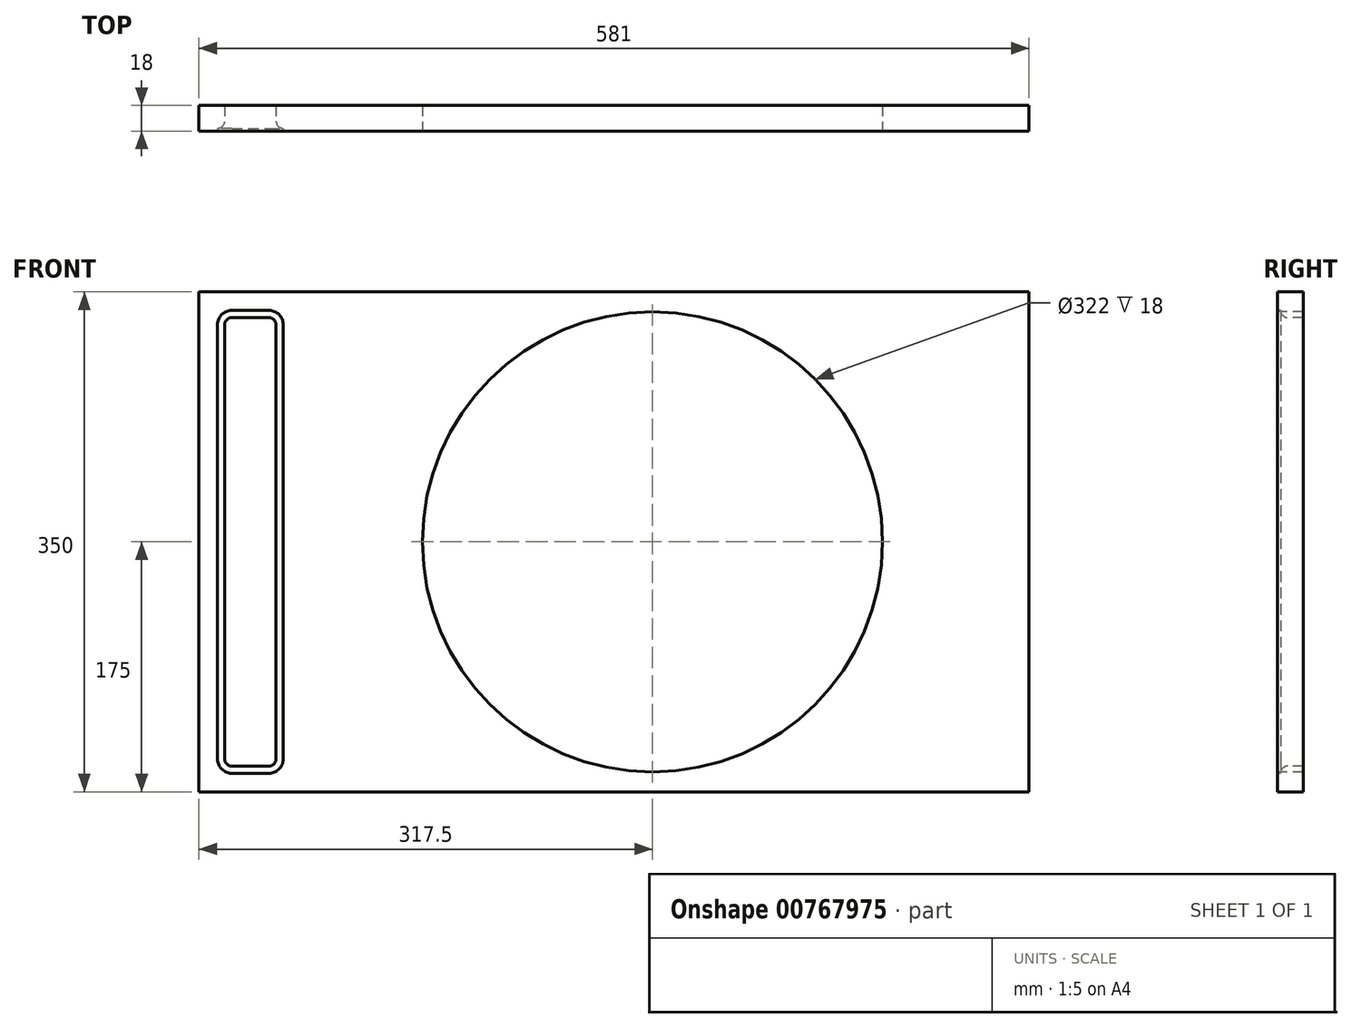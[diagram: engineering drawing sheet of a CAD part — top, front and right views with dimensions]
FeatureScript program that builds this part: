
annotation { "Feature Type Name" : "Feature", "Feature Type Description" : "" }
export const myFeature = defineFeature(function(context is Context, id is Id, definition is map)
    precondition{}
    {
        {
            var Q0;
            Q0=qCreatedBy(makeId("Front.planeOp"),FACE);
            var sketch = newSketch(context, id + "F0", { "sketchPlane" : qUnion([Q0])});
            skLineSegment(sketch, "E0.bottom", {"start": v(-290.5, -175) * mm, "end": v(290.5, -175) * mm});
            skLineSegment(sketch, "E0.top", {"start": v(-290.5, 175) * mm, "end": v(290.5, 175) * mm});
            skLineSegment(sketch, "E0.left", {"start": v(-290.5, -175) * mm, "end": v(-290.5, 175) * mm});
            skLineSegment(sketch, "E0.right", {"start": v(290.5, -175) * mm, "end": v(290.5, 175) * mm});
            skPoint(sketch, "E0.middle", {"position": v(0, 0) * mm});
            skLineSegment(sketch, "E1.bottom", {"start": v(-267.5, 157) * mm, "end": v(-241.5, 157) * mm});
            skLineSegment(sketch, "E1.top", {"start": v(-267.5, -157) * mm, "end": v(-241.5, -157) * mm});
            skLineSegment(sketch, "E1.left", {"start": v(-272.5, 152) * mm, "end": v(-272.5, -152) * mm});
            skLineSegment(sketch, "E1.right", {"start": v(-236.5, 152) * mm, "end": v(-236.5, -152) * mm});
            skLineSegment(sketch, "E2", {"start": v(-236.5, 157) * mm, "end": v(-236.5, 175) * mm, "construction": true});
            skLineSegment(sketch, "E3", {"start": v(-236.5, 175) * mm, "end": v(290.5, -175) * mm, "construction": true});
            skCircle(sketch, "E4", {"center": v(27, 0) * mm, "radius": 161 * mm});
            skPoint(sketch, "E5.visualSharp", {"position": v(-272.5, 157) * mm});
            skArc(sketch, "E5.filletArc", {"start": v(-267.5, 157) * mm, "mid": v(-271.04, 155.54) * mm, "end": v(-272.5, 152) * mm});
            skPoint(sketch, "E6.visualSharp", {"position": v(-236.5, 157) * mm});
            skArc(sketch, "E6.filletArc", {"start": v(-236.5, 152) * mm, "mid": v(-237.96, 155.54) * mm, "end": v(-241.5, 157) * mm});
            skPoint(sketch, "E7.visualSharp", {"position": v(-272.5, -157) * mm});
            skArc(sketch, "E7.filletArc", {"start": v(-272.5, -152) * mm, "mid": v(-271.04, -155.54) * mm, "end": v(-267.5, -157) * mm});
            skPoint(sketch, "E8.visualSharp", {"position": v(-236.5, -157) * mm});
            skArc(sketch, "E8.filletArc", {"start": v(-241.5, -157) * mm, "mid": v(-237.96, -155.54) * mm, "end": v(-236.5, -152) * mm});
            skSolve(sketch);
        }
        {
            var Q0;
            Q0 = qSketchRegion(id + "F0", true);
            extrude(context, id + "F1", {"entities" : qUnion([Q0]), "oppositeDirection" : true, "depth" : 18 * mm, "offsetDistance" : 25 * mm});
        }
        {
            var Q0;
            Q0=makeQuery(id+"F1.opExtrude","CAP_FACE",FACE,{"disambiguationData":[OSD([sQuery(id+"F0.wireOp",EDGE,"E0.bottom"),sQuery(id+"F0.wireOp",EDGE,"E0.top"),sQuery(id+"F0.wireOp",EDGE,"E0.left"),sQuery(id+"F0.wireOp",EDGE,"E0.right"),sQuery(id+"F0.wireOp",EDGE,"E1.bottom"),sQuery(id+"F0.wireOp",EDGE,"E1.top"),sQuery(id+"F0.wireOp",EDGE,"E1.left"),sQuery(id+"F0.wireOp",EDGE,"E1.right"),sQuery(id+"F0.wireOp",EDGE,"E4"),sQuery(id+"F0.wireOp",EDGE,"E5.filletArc"),sQuery(id+"F0.wireOp",EDGE,"E6.filletArc"),sQuery(id+"F0.wireOp",EDGE,"E7.filletArc"),sQuery(id+"F0.wireOp",EDGE,"E8.filletArc")])],"isStart":true});
            var sketch = newSketch(context, id + "F2", { "sketchPlane" : qUnion([Q0])});
            skLineSegment(sketch, "E9.bottom", {"start": v(-267.5, 162) * mm, "end": v(-241.5, 162) * mm});
            skLineSegment(sketch, "E9.top", {"start": v(-267.5, -162) * mm, "end": v(-241.5, -162) * mm});
            skLineSegment(sketch, "E9.left", {"start": v(-277.5, 152) * mm, "end": v(-277.5, -152) * mm});
            skLineSegment(sketch, "E9.right", {"start": v(-231.5, 152) * mm, "end": v(-231.5, -152) * mm});
            skPoint(sketch, "E10.visualSharp", {"position": v(-277.5, 162) * mm});
            skArc(sketch, "E10.filletArc", {"start": v(-267.5, 162) * mm, "mid": v(-274.57, 159.07) * mm, "end": v(-277.5, 152) * mm});
            skPoint(sketch, "E11.visualSharp", {"position": v(-231.5, 162) * mm});
            skArc(sketch, "E11.filletArc", {"start": v(-231.5, 152) * mm, "mid": v(-234.43, 159.07) * mm, "end": v(-241.5, 162) * mm});
            skPoint(sketch, "E12.visualSharp", {"position": v(-277.5, -162) * mm});
            skArc(sketch, "E12.filletArc", {"start": v(-277.5, -152) * mm, "mid": v(-274.57, -159.07) * mm, "end": v(-267.5, -162) * mm});
            skPoint(sketch, "E13.visualSharp", {"position": v(-231.5, -162) * mm});
            skArc(sketch, "E13.filletArc", {"start": v(-241.5, -162) * mm, "mid": v(-234.43, -159.07) * mm, "end": v(-231.5, -152) * mm});
            skSolve(sketch);
        }
        {
            var Q0;
            Q0 = qSketchRegion(id + "F2", true);
            extrude(context, id + "F3", {"entities" : qUnion([Q0]), "operationType" : NewBodyOperationType.REMOVE, "oppositeDirection" : true, "depth" : 2 * mm, "offsetDistance" : 25 * mm});
        }
        {
            var Q0;
            Q0=makeQuery(id+"F3.boolean.opBoolean","INTERSECT",EDGE,{"derivedFrom":[makeQuery(id+"F1.opExtrude","SWEPT_FACE",FACE,{"disambiguationData":[OSD([sQuery(id+"F0.wireOp",EDGE,"E1.top")])]}),makeQuery(id+"F3.opExtrude","CAP_FACE",FACE,{"disambiguationData":[OSD([sQuery(id+"F2.wireOp",EDGE,"E9.bottom"),sQuery(id+"F2.wireOp",EDGE,"E9.top"),sQuery(id+"F2.wireOp",EDGE,"E9.left"),sQuery(id+"F2.wireOp",EDGE,"E9.right"),sQuery(id+"F2.wireOp",EDGE,"E10.filletArc"),sQuery(id+"F2.wireOp",EDGE,"E11.filletArc"),sQuery(id+"F2.wireOp",EDGE,"E12.filletArc"),sQuery(id+"F2.wireOp",EDGE,"E13.filletArc")])],"isStart":false})]});
            var Q1;
            Q1=makeQuery(id+"F3.boolean.opBoolean","INTERSECT",EDGE,{"derivedFrom":[makeQuery(id+"F1.opExtrude","SWEPT_FACE",FACE,{"disambiguationData":[OSD([sQuery(id+"F0.wireOp",EDGE,"E1.left")])]}),makeQuery(id+"F3.opExtrude","CAP_FACE",FACE,{"disambiguationData":[OSD([sQuery(id+"F2.wireOp",EDGE,"E9.bottom"),sQuery(id+"F2.wireOp",EDGE,"E9.top"),sQuery(id+"F2.wireOp",EDGE,"E9.left"),sQuery(id+"F2.wireOp",EDGE,"E9.right"),sQuery(id+"F2.wireOp",EDGE,"E10.filletArc"),sQuery(id+"F2.wireOp",EDGE,"E11.filletArc"),sQuery(id+"F2.wireOp",EDGE,"E12.filletArc"),sQuery(id+"F2.wireOp",EDGE,"E13.filletArc")])],"isStart":false})]});
            var Q2;
            Q2=makeQuery(id+"F3.boolean.opBoolean","INTERSECT",EDGE,{"derivedFrom":[makeQuery(id+"F1.opExtrude","SWEPT_FACE",FACE,{"disambiguationData":[OSD([sQuery(id+"F0.wireOp",EDGE,"E8.filletArc")])]}),makeQuery(id+"F3.opExtrude","CAP_FACE",FACE,{"disambiguationData":[OSD([sQuery(id+"F2.wireOp",EDGE,"E9.bottom"),sQuery(id+"F2.wireOp",EDGE,"E9.top"),sQuery(id+"F2.wireOp",EDGE,"E9.left"),sQuery(id+"F2.wireOp",EDGE,"E9.right"),sQuery(id+"F2.wireOp",EDGE,"E10.filletArc"),sQuery(id+"F2.wireOp",EDGE,"E11.filletArc"),sQuery(id+"F2.wireOp",EDGE,"E12.filletArc"),sQuery(id+"F2.wireOp",EDGE,"E13.filletArc")])],"isStart":false})]});
            var Q3;
            Q3=makeQuery(id+"F3.boolean.opBoolean","INTERSECT",EDGE,{"derivedFrom":[makeQuery(id+"F1.opExtrude","SWEPT_FACE",FACE,{"disambiguationData":[OSD([sQuery(id+"F0.wireOp",EDGE,"E7.filletArc")])]}),makeQuery(id+"F3.opExtrude","CAP_FACE",FACE,{"disambiguationData":[OSD([sQuery(id+"F2.wireOp",EDGE,"E9.bottom"),sQuery(id+"F2.wireOp",EDGE,"E9.top"),sQuery(id+"F2.wireOp",EDGE,"E9.left"),sQuery(id+"F2.wireOp",EDGE,"E9.right"),sQuery(id+"F2.wireOp",EDGE,"E10.filletArc"),sQuery(id+"F2.wireOp",EDGE,"E11.filletArc"),sQuery(id+"F2.wireOp",EDGE,"E12.filletArc"),sQuery(id+"F2.wireOp",EDGE,"E13.filletArc")])],"isStart":false})]});
            var Q4;
            Q4=makeQuery(id+"F3.boolean.opBoolean","INTERSECT",EDGE,{"derivedFrom":[makeQuery(id+"F1.opExtrude","SWEPT_FACE",FACE,{"disambiguationData":[OSD([sQuery(id+"F0.wireOp",EDGE,"E1.right")])]}),makeQuery(id+"F3.opExtrude","CAP_FACE",FACE,{"disambiguationData":[OSD([sQuery(id+"F2.wireOp",EDGE,"E9.bottom"),sQuery(id+"F2.wireOp",EDGE,"E9.top"),sQuery(id+"F2.wireOp",EDGE,"E9.left"),sQuery(id+"F2.wireOp",EDGE,"E9.right"),sQuery(id+"F2.wireOp",EDGE,"E10.filletArc"),sQuery(id+"F2.wireOp",EDGE,"E11.filletArc"),sQuery(id+"F2.wireOp",EDGE,"E12.filletArc"),sQuery(id+"F2.wireOp",EDGE,"E13.filletArc")])],"isStart":false})]});
            var Q5;
            Q5=makeQuery(id+"F3.boolean.opBoolean","INTERSECT",EDGE,{"derivedFrom":[makeQuery(id+"F1.opExtrude","SWEPT_FACE",FACE,{"disambiguationData":[OSD([sQuery(id+"F0.wireOp",EDGE,"E5.filletArc")])]}),makeQuery(id+"F3.opExtrude","CAP_FACE",FACE,{"disambiguationData":[OSD([sQuery(id+"F2.wireOp",EDGE,"E9.bottom"),sQuery(id+"F2.wireOp",EDGE,"E9.top"),sQuery(id+"F2.wireOp",EDGE,"E9.left"),sQuery(id+"F2.wireOp",EDGE,"E9.right"),sQuery(id+"F2.wireOp",EDGE,"E10.filletArc"),sQuery(id+"F2.wireOp",EDGE,"E11.filletArc"),sQuery(id+"F2.wireOp",EDGE,"E12.filletArc"),sQuery(id+"F2.wireOp",EDGE,"E13.filletArc")])],"isStart":false})]});
            var Q6;
            Q6=makeQuery(id+"F3.boolean.opBoolean","INTERSECT",EDGE,{"derivedFrom":[makeQuery(id+"F1.opExtrude","SWEPT_FACE",FACE,{"disambiguationData":[OSD([sQuery(id+"F0.wireOp",EDGE,"E1.bottom")])]}),makeQuery(id+"F3.opExtrude","CAP_FACE",FACE,{"disambiguationData":[OSD([sQuery(id+"F2.wireOp",EDGE,"E9.bottom"),sQuery(id+"F2.wireOp",EDGE,"E9.top"),sQuery(id+"F2.wireOp",EDGE,"E9.left"),sQuery(id+"F2.wireOp",EDGE,"E9.right"),sQuery(id+"F2.wireOp",EDGE,"E10.filletArc"),sQuery(id+"F2.wireOp",EDGE,"E11.filletArc"),sQuery(id+"F2.wireOp",EDGE,"E12.filletArc"),sQuery(id+"F2.wireOp",EDGE,"E13.filletArc")])],"isStart":false})]});
            var Q7;
            Q7=makeQuery(id+"F3.boolean.opBoolean","INTERSECT",EDGE,{"derivedFrom":[makeQuery(id+"F1.opExtrude","SWEPT_FACE",FACE,{"disambiguationData":[OSD([sQuery(id+"F0.wireOp",EDGE,"E6.filletArc")])]}),makeQuery(id+"F3.opExtrude","CAP_FACE",FACE,{"disambiguationData":[OSD([sQuery(id+"F2.wireOp",EDGE,"E9.bottom"),sQuery(id+"F2.wireOp",EDGE,"E9.top"),sQuery(id+"F2.wireOp",EDGE,"E9.left"),sQuery(id+"F2.wireOp",EDGE,"E9.right"),sQuery(id+"F2.wireOp",EDGE,"E10.filletArc"),sQuery(id+"F2.wireOp",EDGE,"E11.filletArc"),sQuery(id+"F2.wireOp",EDGE,"E12.filletArc"),sQuery(id+"F2.wireOp",EDGE,"E13.filletArc")])],"isStart":false})]});
            fillet(context, id + "F4", {"entities" : qUnion([Q0, Q1, Q2, Q3, Q4, Q5, Q6, Q7]), "radius" : 5 * mm, "tangentPropagation" : true, "allowEdgeOverflow" : false});
        }
    });
